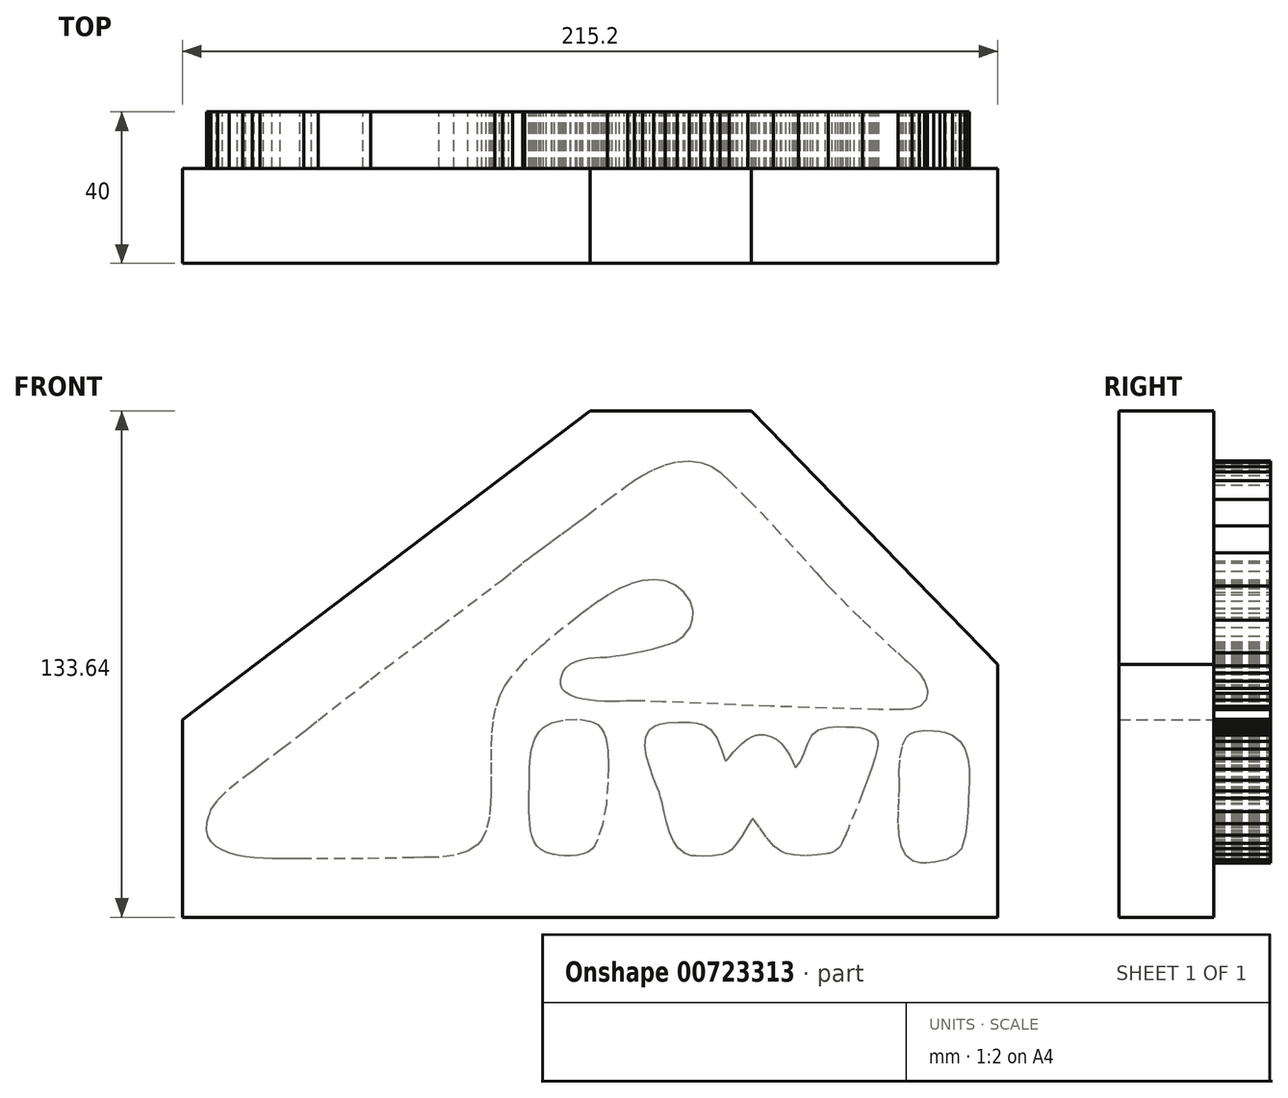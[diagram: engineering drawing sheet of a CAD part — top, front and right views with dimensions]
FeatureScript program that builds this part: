
annotation { "Feature Type Name" : "Feature", "Feature Type Description" : "" }
export const myFeature = defineFeature(function(context is Context, id is Id, definition is map)
    precondition{}
    {
        {
            var Q0;
            Q0=qCreatedBy(makeId("Front.planeOp"),FACE);
            var sketch = newSketch(context, id + "F0", { "sketchPlane" : qUnion([Q0])});
            skLineSegment(sketch, "E0", {"start": v(-15.49, -29.13) * mm, "end": v(-15.48, -28.37) * mm});
            skLineSegment(sketch, "E1", {"start": v(-15.48, -28.37) * mm, "end": v(-15.38, -26.1) * mm});
            skLineSegment(sketch, "E2", {"start": v(-15.38, -26.1) * mm, "end": v(-15, -23.12) * mm});
            skLineSegment(sketch, "E3", {"start": v(-15, -23.12) * mm, "end": v(-14.07, -20.33) * mm});
            skLineSegment(sketch, "E4", {"start": v(-14.07, -20.33) * mm, "end": v(-12.87, -18.4) * mm});
            skLineSegment(sketch, "E5", {"start": v(-12.87, -18.4) * mm, "end": v(-12.36, -17.88) * mm});
            skLineSegment(sketch, "E6", {"start": v(-12.36, -17.88) * mm, "end": v(-11.78, -17.29) * mm});
            skLineSegment(sketch, "E7", {"start": v(-11.78, -17.29) * mm, "end": v(-9.5, -16.05) * mm});
            skLineSegment(sketch, "E8", {"start": v(-9.5, -16.05) * mm, "end": v(-5.9, -15.18) * mm});
            skLineSegment(sketch, "E9", {"start": v(-5.9, -15.18) * mm, "end": v(-2.13, -15.15) * mm});
            skLineSegment(sketch, "E10", {"start": v(-2.13, -15.15) * mm, "end": v(0.44, -15.56) * mm});
            skLineSegment(sketch, "E11", {"start": v(0.44, -15.56) * mm, "end": v(1.25, -15.83) * mm});
            skLineSegment(sketch, "E12", {"start": v(1.25, -15.83) * mm, "end": v(1.59, -15.94) * mm});
            skLineSegment(sketch, "E13", {"start": v(1.59, -15.94) * mm, "end": v(2.5, -16.5) * mm});
            skLineSegment(sketch, "E14", {"start": v(2.5, -16.5) * mm, "end": v(3.48, -17.52) * mm});
            skLineSegment(sketch, "E15", {"start": v(3.48, -17.52) * mm, "end": v(4.2, -18.8) * mm});
            skLineSegment(sketch, "E16", {"start": v(4.2, -18.8) * mm, "end": v(4.7, -20.25) * mm});
            skLineSegment(sketch, "E17", {"start": v(4.7, -20.25) * mm, "end": v(5.02, -21.82) * mm});
            skLineSegment(sketch, "E18", {"start": v(5.02, -21.82) * mm, "end": v(5.2, -23.41) * mm});
            skLineSegment(sketch, "E19", {"start": v(5.2, -23.41) * mm, "end": v(5.3, -24.95) * mm});
            skLineSegment(sketch, "E20", {"start": v(5.3, -24.95) * mm, "end": v(5.32, -26) * mm});
            skLineSegment(sketch, "E21", {"start": v(5.32, -26) * mm, "end": v(5.32, -26.35) * mm});
            skLineSegment(sketch, "E22", {"start": v(5.32, -26.35) * mm, "end": v(5.32, -27.7) * mm});
            skLineSegment(sketch, "E23", {"start": v(5.32, -27.7) * mm, "end": v(5.23, -31.79) * mm});
            skLineSegment(sketch, "E24", {"start": v(5.23, -31.79) * mm, "end": v(4.8, -37.42) * mm});
            skLineSegment(sketch, "E25", {"start": v(4.8, -37.42) * mm, "end": v(3.78, -42.93) * mm});
            skLineSegment(sketch, "E26", {"start": v(3.78, -42.93) * mm, "end": v(2.53, -46.82) * mm});
            skLineSegment(sketch, "E27", {"start": v(2.53, -46.82) * mm, "end": v(1.95, -48.03) * mm});
            skLineSegment(sketch, "E28", {"start": v(1.95, -48.03) * mm, "end": v(1.8, -48.36) * mm});
            skLineSegment(sketch, "E29", {"start": v(1.8, -48.36) * mm, "end": v(1.11, -49.23) * mm});
            skLineSegment(sketch, "E30", {"start": v(1.11, -49.23) * mm, "end": v(-0.02, -50.1) * mm});
            skLineSegment(sketch, "E31", {"start": v(-0.02, -50.1) * mm, "end": v(-1.38, -50.7) * mm});
            skLineSegment(sketch, "E32", {"start": v(-1.38, -50.7) * mm, "end": v(-2.9, -51.06) * mm});
            skLineSegment(sketch, "E33", {"start": v(-2.9, -51.06) * mm, "end": v(-4.5, -51.2) * mm});
            skLineSegment(sketch, "E34", {"start": v(-4.5, -51.2) * mm, "end": v(-6.14, -51.18) * mm});
            skLineSegment(sketch, "E35", {"start": v(-6.14, -51.18) * mm, "end": v(-7.74, -51.03) * mm});
            skLineSegment(sketch, "E36", {"start": v(-7.74, -51.03) * mm, "end": v(-8.85, -50.86) * mm});
            skLineSegment(sketch, "E37", {"start": v(-8.85, -50.86) * mm, "end": v(-9.21, -50.79) * mm});
            skLineSegment(sketch, "E38", {"start": v(-9.21, -50.79) * mm, "end": v(-9.68, -50.7) * mm});
            skLineSegment(sketch, "E39", {"start": v(-9.68, -50.7) * mm, "end": v(-11.03, -50.25) * mm});
            skLineSegment(sketch, "E40", {"start": v(-11.03, -50.25) * mm, "end": v(-12.44, -49.48) * mm});
            skLineSegment(sketch, "E41", {"start": v(-12.44, -49.48) * mm, "end": v(-13.5, -48.48) * mm});
            skLineSegment(sketch, "E42", {"start": v(-13.5, -48.48) * mm, "end": v(-14.28, -47.28) * mm});
            skLineSegment(sketch, "E43", {"start": v(-14.28, -47.28) * mm, "end": v(-14.82, -45.9) * mm});
            skLineSegment(sketch, "E44", {"start": v(-14.82, -45.9) * mm, "end": v(-15.16, -44.37) * mm});
            skLineSegment(sketch, "E45", {"start": v(-15.16, -44.37) * mm, "end": v(-15.37, -42.7) * mm});
            skLineSegment(sketch, "E46", {"start": v(-15.37, -42.7) * mm, "end": v(-15.48, -41.36) * mm});
            skLineSegment(sketch, "E47", {"start": v(-15.48, -41.36) * mm, "end": v(-15.5, -40.9) * mm});
            skLineSegment(sketch, "E48", {"start": v(-15.5, -40.9) * mm, "end": v(-15.52, -40.68) * mm});
            skLineSegment(sketch, "E49", {"start": v(-15.52, -40.68) * mm, "end": v(-15.53, -39.98) * mm});
            skLineSegment(sketch, "E50", {"start": v(-15.53, -39.98) * mm, "end": v(-15.54, -38.53) * mm});
            skLineSegment(sketch, "E51", {"start": v(-15.54, -38.53) * mm, "end": v(-15.54, -36.74) * mm});
            skLineSegment(sketch, "E52", {"start": v(-15.54, -36.74) * mm, "end": v(-15.54, -34.79) * mm});
            skLineSegment(sketch, "E53", {"start": v(-15.54, -34.79) * mm, "end": v(-15.52, -32.86) * mm});
            skLineSegment(sketch, "E54", {"start": v(-15.52, -32.86) * mm, "end": v(-15.51, -31.16) * mm});
            skLineSegment(sketch, "E55", {"start": v(-15.51, -31.16) * mm, "end": v(-15.5, -29.85) * mm});
            skLineSegment(sketch, "E56", {"start": v(-15.5, -29.85) * mm, "end": v(-15.49, -29.3) * mm});
            skLineSegment(sketch, "E57", {"start": v(-15.49, -29.3) * mm, "end": v(-15.49, -29.13) * mm});
            skLineSegment(sketch, "E58", {"start": v(84.47, -19.48) * mm, "end": v(84.82, -19.11) * mm});
            skLineSegment(sketch, "E59", {"start": v(84.82, -19.11) * mm, "end": v(86.32, -18.4) * mm});
            skLineSegment(sketch, "E60", {"start": v(86.32, -18.4) * mm, "end": v(88.7, -18.05) * mm});
            skLineSegment(sketch, "E61", {"start": v(88.7, -18.05) * mm, "end": v(91.21, -18.14) * mm});
            skLineSegment(sketch, "E62", {"start": v(91.21, -18.14) * mm, "end": v(92.88, -18.35) * mm});
            skLineSegment(sketch, "E63", {"start": v(92.88, -18.35) * mm, "end": v(93.44, -18.43) * mm});
            skLineSegment(sketch, "E64", {"start": v(93.44, -18.43) * mm, "end": v(94.15, -18.54) * mm});
            skLineSegment(sketch, "E65", {"start": v(94.15, -18.54) * mm, "end": v(96.21, -19.32) * mm});
            skLineSegment(sketch, "E66", {"start": v(96.21, -19.32) * mm, "end": v(98.19, -20.9) * mm});
            skLineSegment(sketch, "E67", {"start": v(98.19, -20.9) * mm, "end": v(99.5, -23.04) * mm});
            skLineSegment(sketch, "E68", {"start": v(99.5, -23.04) * mm, "end": v(100.25, -25.57) * mm});
            skLineSegment(sketch, "E69", {"start": v(100.25, -25.57) * mm, "end": v(100.6, -28.34) * mm});
            skLineSegment(sketch, "E70", {"start": v(100.6, -28.34) * mm, "end": v(100.65, -31.19) * mm});
            skLineSegment(sketch, "E71", {"start": v(100.65, -31.19) * mm, "end": v(100.54, -33.97) * mm});
            skLineSegment(sketch, "E72", {"start": v(100.54, -33.97) * mm, "end": v(100.43, -35.9) * mm});
            skLineSegment(sketch, "E73", {"start": v(100.43, -35.9) * mm, "end": v(100.4, -36.54) * mm});
            skLineSegment(sketch, "E74", {"start": v(100.4, -36.54) * mm, "end": v(100.36, -37.28) * mm});
            skLineSegment(sketch, "E75", {"start": v(100.36, -37.28) * mm, "end": v(100.25, -39.52) * mm});
            skLineSegment(sketch, "E76", {"start": v(100.25, -39.52) * mm, "end": v(100.02, -42.64) * mm});
            skLineSegment(sketch, "E77", {"start": v(100.02, -42.64) * mm, "end": v(99.57, -45.71) * mm});
            skLineSegment(sketch, "E78", {"start": v(99.57, -45.71) * mm, "end": v(99.03, -47.89) * mm});
            skLineSegment(sketch, "E79", {"start": v(99.03, -47.89) * mm, "end": v(98.76, -48.58) * mm});
            skLineSegment(sketch, "E80", {"start": v(98.76, -48.58) * mm, "end": v(98.52, -49.22) * mm});
            skLineSegment(sketch, "E81", {"start": v(98.52, -49.22) * mm, "end": v(97.1, -50.85) * mm});
            skLineSegment(sketch, "E82", {"start": v(97.1, -50.85) * mm, "end": v(94.51, -52.21) * mm});
            skLineSegment(sketch, "E83", {"start": v(94.51, -52.21) * mm, "end": v(91.5, -52.89) * mm});
            skLineSegment(sketch, "E84", {"start": v(91.5, -52.89) * mm, "end": v(89.28, -53.08) * mm});
            skLineSegment(sketch, "E85", {"start": v(89.28, -53.08) * mm, "end": v(88.53, -53.1) * mm});
            skLineSegment(sketch, "E86", {"start": v(88.53, -53.1) * mm, "end": v(87.84, -53.11) * mm});
            skLineSegment(sketch, "E87", {"start": v(87.84, -53.11) * mm, "end": v(85.76, -52.58) * mm});
            skLineSegment(sketch, "E88", {"start": v(85.76, -52.58) * mm, "end": v(83.87, -51.05) * mm});
            skLineSegment(sketch, "E89", {"start": v(83.87, -51.05) * mm, "end": v(82.7, -48.7) * mm});
            skLineSegment(sketch, "E90", {"start": v(82.7, -48.7) * mm, "end": v(82.08, -45.78) * mm});
            skLineSegment(sketch, "E91", {"start": v(82.08, -45.78) * mm, "end": v(81.87, -42.5) * mm});
            skLineSegment(sketch, "E92", {"start": v(81.87, -42.5) * mm, "end": v(81.92, -39.06) * mm});
            skLineSegment(sketch, "E93", {"start": v(81.92, -39.06) * mm, "end": v(82.06, -35.7) * mm});
            skLineSegment(sketch, "E94", {"start": v(82.06, -35.7) * mm, "end": v(82.14, -33.41) * mm});
            skLineSegment(sketch, "E95", {"start": v(82.14, -33.41) * mm, "end": v(82.14, -32.65) * mm});
            skLineSegment(sketch, "E96", {"start": v(82.14, -32.65) * mm, "end": v(82.14, -31.7) * mm});
            skLineSegment(sketch, "E97", {"start": v(82.14, -31.7) * mm, "end": v(82.13, -28.87) * mm});
            skLineSegment(sketch, "E98", {"start": v(82.13, -28.87) * mm, "end": v(82.31, -25.24) * mm});
            skLineSegment(sketch, "E99", {"start": v(82.31, -25.24) * mm, "end": v(83, -22.02) * mm});
            skLineSegment(sketch, "E100", {"start": v(83, -22.02) * mm, "end": v(83.98, -20) * mm});
            skLineSegment(sketch, "E101", {"start": v(83.98, -20) * mm, "end": v(84.47, -19.48) * mm});
            skLineSegment(sketch, "E102", {"start": v(27.66, 13.43) * mm, "end": v(27.59, 14.13) * mm});
            skLineSegment(sketch, "E103", {"start": v(27.59, 14.13) * mm, "end": v(26.9, 16.16) * mm});
            skLineSegment(sketch, "E104", {"start": v(26.9, 16.16) * mm, "end": v(25.36, 18.47) * mm});
            skLineSegment(sketch, "E105", {"start": v(25.36, 18.47) * mm, "end": v(23.2, 20.21) * mm});
            skLineSegment(sketch, "E106", {"start": v(23.2, 20.21) * mm, "end": v(21.25, 21.11) * mm});
            skLineSegment(sketch, "E107", {"start": v(21.25, 21.11) * mm, "end": v(20.57, 21.27) * mm});
            skLineSegment(sketch, "E108", {"start": v(20.57, 21.27) * mm, "end": v(19.79, 21.46) * mm});
            skLineSegment(sketch, "E109", {"start": v(19.79, 21.46) * mm, "end": v(17.37, 21.68) * mm});
            skLineSegment(sketch, "E110", {"start": v(17.37, 21.68) * mm, "end": v(14.24, 21.42) * mm});
            skLineSegment(sketch, "E111", {"start": v(14.24, 21.42) * mm, "end": v(11.22, 20.61) * mm});
            skLineSegment(sketch, "E112", {"start": v(11.22, 20.61) * mm, "end": v(8.3, 19.37) * mm});
            skLineSegment(sketch, "E113", {"start": v(8.3, 19.37) * mm, "end": v(5.49, 17.82) * mm});
            skLineSegment(sketch, "E114", {"start": v(5.49, 17.82) * mm, "end": v(2.8, 16.08) * mm});
            skLineSegment(sketch, "E115", {"start": v(2.8, 16.08) * mm, "end": v(0.27, 14.25) * mm});
            skLineSegment(sketch, "E116", {"start": v(0.27, 14.25) * mm, "end": v(-1.51, 12.91) * mm});
            skLineSegment(sketch, "E117", {"start": v(-1.51, 12.91) * mm, "end": v(-2.1, 12.46) * mm});
            skLineSegment(sketch, "E118", {"start": v(-2.1, 12.46) * mm, "end": v(-2.94, 11.84) * mm});
            skLineSegment(sketch, "E119", {"start": v(-2.94, 11.84) * mm, "end": v(-11.04, 5.29) * mm});
            skLineSegment(sketch, "E120", {"start": v(-11.04, 5.29) * mm, "end": v(-11.83, 4.63) * mm});
            skLineSegment(sketch, "E121", {"start": v(-11.83, 4.63) * mm, "end": v(-12.72, 3.9) * mm});
            skLineSegment(sketch, "E122", {"start": v(-12.72, 3.9) * mm, "end": v(-17.1, -0.15) * mm});
            skLineSegment(sketch, "E123", {"start": v(-17.1, -0.15) * mm, "end": v(-20.97, -4.65) * mm});
            skLineSegment(sketch, "E124", {"start": v(-20.97, -4.65) * mm, "end": v(-21.6, -5.62) * mm});
            skLineSegment(sketch, "E125", {"start": v(-21.6, -5.62) * mm, "end": v(-22.09, -6.38) * mm});
            skLineSegment(sketch, "E126", {"start": v(-22.09, -6.38) * mm, "end": v(-23.3, -8.85) * mm});
            skLineSegment(sketch, "E127", {"start": v(-23.3, -8.85) * mm, "end": v(-24.46, -12.24) * mm});
            skLineSegment(sketch, "E128", {"start": v(-24.46, -12.24) * mm, "end": v(-25.16, -15.74) * mm});
            skLineSegment(sketch, "E129", {"start": v(-25.16, -15.74) * mm, "end": v(-25.52, -19.33) * mm});
            skLineSegment(sketch, "E130", {"start": v(-25.52, -19.33) * mm, "end": v(-25.63, -22.96) * mm});
            skLineSegment(sketch, "E131", {"start": v(-25.63, -22.96) * mm, "end": v(-25.61, -26.6) * mm});
            skLineSegment(sketch, "E132", {"start": v(-25.61, -26.6) * mm, "end": v(-25.57, -30.23) * mm});
            skLineSegment(sketch, "E133", {"start": v(-25.57, -30.23) * mm, "end": v(-25.59, -32.9) * mm});
            skLineSegment(sketch, "E134", {"start": v(-25.59, -32.9) * mm, "end": v(-25.62, -33.79) * mm});
            skLineSegment(sketch, "E135", {"start": v(-25.62, -33.79) * mm, "end": v(-25.65, -34.66) * mm});
            skLineSegment(sketch, "E136", {"start": v(-25.65, -34.66) * mm, "end": v(-25.73, -37.29) * mm});
            skLineSegment(sketch, "E137", {"start": v(-25.73, -37.29) * mm, "end": v(-26.05, -40.94) * mm});
            skLineSegment(sketch, "E138", {"start": v(-26.05, -40.94) * mm, "end": v(-26.9, -44.44) * mm});
            skLineSegment(sketch, "E139", {"start": v(-26.9, -44.44) * mm, "end": v(-28.06, -46.83) * mm});
            skLineSegment(sketch, "E140", {"start": v(-28.06, -46.83) * mm, "end": v(-28.6, -47.5) * mm});
            skLineSegment(sketch, "E141", {"start": v(-28.6, -47.5) * mm, "end": v(-29.2, -48.23) * mm});
            skLineSegment(sketch, "E142", {"start": v(-29.2, -48.23) * mm, "end": v(-31.67, -49.9) * mm});
            skLineSegment(sketch, "E143", {"start": v(-31.67, -49.9) * mm, "end": v(-35.39, -51.1) * mm});
            skLineSegment(sketch, "E144", {"start": v(-35.39, -51.1) * mm, "end": v(-39.38, -51.5) * mm});
            skLineSegment(sketch, "E145", {"start": v(-39.38, -51.5) * mm, "end": v(-42.28, -51.59) * mm});
            skLineSegment(sketch, "E146", {"start": v(-42.28, -51.59) * mm, "end": v(-43.25, -51.62) * mm});
            skLineSegment(sketch, "E147", {"start": v(-43.25, -51.62) * mm, "end": v(-45.96, -51.7) * mm});
            skLineSegment(sketch, "E148", {"start": v(-45.96, -51.7) * mm, "end": v(-59.46, -51.96) * mm});
            skLineSegment(sketch, "E149", {"start": v(-59.46, -51.96) * mm, "end": v(-72.97, -52) * mm});
            skLineSegment(sketch, "E150", {"start": v(-72.97, -52) * mm, "end": v(-75.69, -51.95) * mm});
            skLineSegment(sketch, "E151", {"start": v(-75.69, -51.95) * mm, "end": v(-76.08, -51.94) * mm});
            skLineSegment(sketch, "E152", {"start": v(-76.08, -51.94) * mm, "end": v(-77.27, -51.94) * mm});
            skLineSegment(sketch, "E153", {"start": v(-77.27, -51.94) * mm, "end": v(-79.12, -51.96) * mm});
            skLineSegment(sketch, "E154", {"start": v(-79.12, -51.96) * mm, "end": v(-81.2, -51.96) * mm});
            skLineSegment(sketch, "E155", {"start": v(-81.2, -51.96) * mm, "end": v(-83.41, -51.93) * mm});
            skLineSegment(sketch, "E156", {"start": v(-83.41, -51.93) * mm, "end": v(-85.72, -51.85) * mm});
            skLineSegment(sketch, "E157", {"start": v(-85.72, -51.85) * mm, "end": v(-88.06, -51.68) * mm});
            skLineSegment(sketch, "E158", {"start": v(-88.06, -51.68) * mm, "end": v(-90.38, -51.4) * mm});
            skLineSegment(sketch, "E159", {"start": v(-90.38, -51.4) * mm, "end": v(-92.6, -51) * mm});
            skLineSegment(sketch, "E160", {"start": v(-92.6, -51) * mm, "end": v(-94.67, -50.43) * mm});
            skLineSegment(sketch, "E161", {"start": v(-94.67, -50.43) * mm, "end": v(-96.53, -49.69) * mm});
            skLineSegment(sketch, "E162", {"start": v(-96.53, -49.69) * mm, "end": v(-98.12, -48.73) * mm});
            skLineSegment(sketch, "E163", {"start": v(-98.12, -48.73) * mm, "end": v(-99.38, -47.54) * mm});
            skLineSegment(sketch, "E164", {"start": v(-99.38, -47.54) * mm, "end": v(-100.24, -46.1) * mm});
            skLineSegment(sketch, "E165", {"start": v(-100.24, -46.1) * mm, "end": v(-100.65, -44.37) * mm});
            skLineSegment(sketch, "E166", {"start": v(-100.65, -44.37) * mm, "end": v(-100.54, -42.34) * mm});
            skLineSegment(sketch, "E167", {"start": v(-100.54, -42.34) * mm, "end": v(-100.08, -40.55) * mm});
            skLineSegment(sketch, "E168", {"start": v(-100.08, -40.55) * mm, "end": v(-99.85, -39.98) * mm});
            skLineSegment(sketch, "E169", {"start": v(-99.85, -39.98) * mm, "end": v(-99.48, -39.02) * mm});
            skLineSegment(sketch, "E170", {"start": v(-99.48, -39.02) * mm, "end": v(-97.72, -36.4) * mm});
            skLineSegment(sketch, "E171", {"start": v(-97.72, -36.4) * mm, "end": v(-94.67, -33.35) * mm});
            skLineSegment(sketch, "E172", {"start": v(-94.67, -33.35) * mm, "end": v(-91.2, -30.65) * mm});
            skLineSegment(sketch, "E173", {"start": v(-91.2, -30.65) * mm, "end": v(-88.62, -28.77) * mm});
            skLineSegment(sketch, "E174", {"start": v(-88.62, -28.77) * mm, "end": v(-87.78, -28.12) * mm});
            skLineSegment(sketch, "E175", {"start": v(-87.78, -28.12) * mm, "end": v(-86.64, -27.23) * mm});
            skLineSegment(sketch, "E176", {"start": v(-86.64, -27.23) * mm, "end": v(-80.82, -22.86) * mm});
            skLineSegment(sketch, "E177", {"start": v(-80.82, -22.86) * mm, "end": v(-75.05, -18.44) * mm});
            skLineSegment(sketch, "E178", {"start": v(-75.05, -18.44) * mm, "end": v(-73.92, -17.53) * mm});
            skLineSegment(sketch, "E179", {"start": v(-73.92, -17.53) * mm, "end": v(-71.2, -15.32) * mm});
            skLineSegment(sketch, "E180", {"start": v(-71.2, -15.32) * mm, "end": v(-57.33, -4.54) * mm});
            skLineSegment(sketch, "E181", {"start": v(-57.33, -4.54) * mm, "end": v(-43.32, 6.08) * mm});
            skLineSegment(sketch, "E182", {"start": v(-43.32, 6.08) * mm, "end": v(-40.53, 8.2) * mm});
            skLineSegment(sketch, "E183", {"start": v(-40.53, 8.2) * mm, "end": v(-39.08, 9.3) * mm});
            skLineSegment(sketch, "E184", {"start": v(-39.08, 9.3) * mm, "end": v(-24.57, 20.28) * mm});
            skLineSegment(sketch, "E185", {"start": v(-24.57, 20.28) * mm, "end": v(-23.11, 21.36) * mm});
            skLineSegment(sketch, "E186", {"start": v(-23.11, 21.36) * mm, "end": v(-22.6, 21.74) * mm});
            skLineSegment(sketch, "E187", {"start": v(-22.6, 21.74) * mm, "end": v(-19.85, 23.99) * mm});
            skLineSegment(sketch, "E188", {"start": v(-19.85, 23.99) * mm, "end": v(-17.28, 26.15) * mm});
            skLineSegment(sketch, "E189", {"start": v(-17.28, 26.15) * mm, "end": v(-16.85, 26.48) * mm});
            skLineSegment(sketch, "E190", {"start": v(-16.85, 26.48) * mm, "end": v(-16.69, 26.6) * mm});
            skLineSegment(sketch, "E191", {"start": v(-16.69, 26.6) * mm, "end": v(-16.08, 27.06) * mm});
            skLineSegment(sketch, "E192", {"start": v(-16.08, 27.06) * mm, "end": v(-14.42, 28.29) * mm});
            skLineSegment(sketch, "E193", {"start": v(-14.42, 28.29) * mm, "end": v(-12.16, 29.95) * mm});
            skLineSegment(sketch, "E194", {"start": v(-12.16, 29.95) * mm, "end": v(-9.57, 31.86) * mm});
            skLineSegment(sketch, "E195", {"start": v(-9.57, 31.86) * mm, "end": v(-6.91, 33.82) * mm});
            skLineSegment(sketch, "E196", {"start": v(-6.91, 33.82) * mm, "end": v(-4.46, 35.62) * mm});
            skLineSegment(sketch, "E197", {"start": v(-4.46, 35.62) * mm, "end": v(-2.5, 37.07) * mm});
            skLineSegment(sketch, "E198", {"start": v(-2.5, 37.07) * mm, "end": v(-1.59, 37.74) * mm});
            skLineSegment(sketch, "E199", {"start": v(-1.59, 37.74) * mm, "end": v(-1.29, 37.97) * mm});
            skLineSegment(sketch, "E200", {"start": v(-1.29, 37.97) * mm, "end": v(-0.21, 38.77) * mm});
            skLineSegment(sketch, "E201", {"start": v(-0.21, 38.77) * mm, "end": v(5.1, 42.8) * mm});
            skLineSegment(sketch, "E202", {"start": v(5.1, 42.8) * mm, "end": v(10.48, 46.73) * mm});
            skLineSegment(sketch, "E203", {"start": v(10.48, 46.73) * mm, "end": v(11.6, 47.48) * mm});
            skLineSegment(sketch, "E204", {"start": v(11.6, 47.48) * mm, "end": v(12.27, 47.94) * mm});
            skLineSegment(sketch, "E205", {"start": v(12.27, 47.94) * mm, "end": v(14.38, 49.24) * mm});
            skLineSegment(sketch, "E206", {"start": v(14.38, 49.24) * mm, "end": v(17.34, 50.79) * mm});
            skLineSegment(sketch, "E207", {"start": v(17.34, 50.79) * mm, "end": v(20.41, 52.03) * mm});
            skLineSegment(sketch, "E208", {"start": v(20.41, 52.03) * mm, "end": v(23.55, 52.84) * mm});
            skLineSegment(sketch, "E209", {"start": v(23.55, 52.84) * mm, "end": v(26.68, 53.11) * mm});
            skLineSegment(sketch, "E210", {"start": v(26.68, 53.11) * mm, "end": v(29.75, 52.73) * mm});
            skLineSegment(sketch, "E211", {"start": v(29.75, 52.73) * mm, "end": v(32.7, 51.58) * mm});
            skLineSegment(sketch, "E212", {"start": v(32.7, 51.58) * mm, "end": v(34.83, 50.14) * mm});
            skLineSegment(sketch, "E213", {"start": v(34.83, 50.14) * mm, "end": v(35.45, 49.56) * mm});
            skLineSegment(sketch, "E214", {"start": v(35.45, 49.56) * mm, "end": v(37.18, 47.92) * mm});
            skLineSegment(sketch, "E215", {"start": v(37.18, 47.92) * mm, "end": v(42.25, 42.88) * mm});
            skLineSegment(sketch, "E216", {"start": v(42.25, 42.88) * mm, "end": v(48.96, 35.9) * mm});
            skLineSegment(sketch, "E217", {"start": v(48.96, 35.9) * mm, "end": v(55.5, 28.84) * mm});
            skLineSegment(sketch, "E218", {"start": v(55.5, 28.84) * mm, "end": v(60.2, 23.62) * mm});
            skLineSegment(sketch, "E219", {"start": v(60.2, 23.62) * mm, "end": v(61.77, 21.88) * mm});
            skLineSegment(sketch, "E220", {"start": v(61.77, 21.88) * mm, "end": v(63.44, 20.02) * mm});
            skLineSegment(sketch, "E221", {"start": v(63.44, 20.02) * mm, "end": v(72.41, 11) * mm});
            skLineSegment(sketch, "E222", {"start": v(72.41, 11) * mm, "end": v(81.77, 2.35) * mm});
            skLineSegment(sketch, "E223", {"start": v(81.77, 2.35) * mm, "end": v(83.63, 0.68) * mm});
            skLineSegment(sketch, "E224", {"start": v(83.63, 0.68) * mm, "end": v(84.11, 0.25) * mm});
            skLineSegment(sketch, "E225", {"start": v(84.11, 0.25) * mm, "end": v(85.56, -1.06) * mm});
            skLineSegment(sketch, "E226", {"start": v(85.56, -1.06) * mm, "end": v(87.4, -2.98) * mm});
            skLineSegment(sketch, "E227", {"start": v(87.4, -2.98) * mm, "end": v(88.82, -5.14) * mm});
            skLineSegment(sketch, "E228", {"start": v(88.82, -5.14) * mm, "end": v(89.47, -7) * mm});
            skLineSegment(sketch, "E229", {"start": v(89.47, -7) * mm, "end": v(89.53, -7.63) * mm});
            skLineSegment(sketch, "E230", {"start": v(89.53, -7.63) * mm, "end": v(89.59, -8.23) * mm});
            skLineSegment(sketch, "E231", {"start": v(89.59, -8.23) * mm, "end": v(89.16, -10.1) * mm});
            skLineSegment(sketch, "E232", {"start": v(89.16, -10.1) * mm, "end": v(87.68, -11.63) * mm});
            skLineSegment(sketch, "E233", {"start": v(87.68, -11.63) * mm, "end": v(85.37, -12.4) * mm});
            skLineSegment(sketch, "E234", {"start": v(85.37, -12.4) * mm, "end": v(83.22, -12.62) * mm});
            skLineSegment(sketch, "E235", {"start": v(83.22, -12.62) * mm, "end": v(82.51, -12.61) * mm});
            skLineSegment(sketch, "E236", {"start": v(82.51, -12.61) * mm, "end": v(76.8, -12.56) * mm});
            skLineSegment(sketch, "E237", {"start": v(76.8, -12.56) * mm, "end": v(48.17, -11.7) * mm});
            skLineSegment(sketch, "E238", {"start": v(48.17, -11.7) * mm, "end": v(19.58, -10.48) * mm});
            skLineSegment(sketch, "E239", {"start": v(19.58, -10.48) * mm, "end": v(13.87, -10.26) * mm});
            skLineSegment(sketch, "E240", {"start": v(13.87, -10.26) * mm, "end": v(13.63, -10.25) * mm});
            skLineSegment(sketch, "E241", {"start": v(13.63, -10.25) * mm, "end": v(12.9, -10.26) * mm});
            skLineSegment(sketch, "E242", {"start": v(12.9, -10.26) * mm, "end": v(11.61, -10.29) * mm});
            skLineSegment(sketch, "E243", {"start": v(11.61, -10.29) * mm, "end": v(10.05, -10.33) * mm});
            skLineSegment(sketch, "E244", {"start": v(10.05, -10.33) * mm, "end": v(8.29, -10.37) * mm});
            skLineSegment(sketch, "E245", {"start": v(8.29, -10.37) * mm, "end": v(6.38, -10.39) * mm});
            skLineSegment(sketch, "E246", {"start": v(6.38, -10.39) * mm, "end": v(4.38, -10.35) * mm});
            skLineSegment(sketch, "E247", {"start": v(4.38, -10.35) * mm, "end": v(2.37, -10.25) * mm});
            skLineSegment(sketch, "E248", {"start": v(2.37, -10.25) * mm, "end": v(0.4, -10.07) * mm});
            skLineSegment(sketch, "E249", {"start": v(0.4, -10.07) * mm, "end": v(-1.48, -9.77) * mm});
            skLineSegment(sketch, "E250", {"start": v(-1.48, -9.77) * mm, "end": v(-3.2, -9.34) * mm});
            skLineSegment(sketch, "E251", {"start": v(-3.2, -9.34) * mm, "end": v(-4.7, -8.77) * mm});
            skLineSegment(sketch, "E252", {"start": v(-4.7, -8.77) * mm, "end": v(-5.9, -8.02) * mm});
            skLineSegment(sketch, "E253", {"start": v(-5.9, -8.02) * mm, "end": v(-6.77, -7.08) * mm});
            skLineSegment(sketch, "E254", {"start": v(-6.77, -7.08) * mm, "end": v(-7.24, -5.93) * mm});
            skLineSegment(sketch, "E255", {"start": v(-7.24, -5.93) * mm, "end": v(-7.24, -4.54) * mm});
            skLineSegment(sketch, "E256", {"start": v(-7.24, -4.54) * mm, "end": v(-6.88, -3.3) * mm});
            skLineSegment(sketch, "E257", {"start": v(-6.88, -3.3) * mm, "end": v(-6.7, -2.9) * mm});
            skLineSegment(sketch, "E258", {"start": v(-6.7, -2.9) * mm, "end": v(-6.54, -2.54) * mm});
            skLineSegment(sketch, "E259", {"start": v(-6.54, -2.54) * mm, "end": v(-5.82, -1.54) * mm});
            skLineSegment(sketch, "E260", {"start": v(-5.82, -1.54) * mm, "end": v(-4.63, -0.53) * mm});
            skLineSegment(sketch, "E261", {"start": v(-4.63, -0.53) * mm, "end": v(-3.22, 0.18) * mm});
            skLineSegment(sketch, "E262", {"start": v(-3.22, 0.18) * mm, "end": v(-1.65, 0.66) * mm});
            skLineSegment(sketch, "E263", {"start": v(-1.65, 0.66) * mm, "end": v(0, 0.95) * mm});
            skLineSegment(sketch, "E264", {"start": v(0, 0.95) * mm, "end": v(1.66, 1.12) * mm});
            skLineSegment(sketch, "E265", {"start": v(1.66, 1.12) * mm, "end": v(3.27, 1.2) * mm});
            skLineSegment(sketch, "E266", {"start": v(3.27, 1.2) * mm, "end": v(4.37, 1.26) * mm});
            skLineSegment(sketch, "E267", {"start": v(4.37, 1.26) * mm, "end": v(4.73, 1.28) * mm});
            skLineSegment(sketch, "E268", {"start": v(4.73, 1.28) * mm, "end": v(4.99, 1.3) * mm});
            skLineSegment(sketch, "E269", {"start": v(4.99, 1.3) * mm, "end": v(5.75, 1.38) * mm});
            skLineSegment(sketch, "E270", {"start": v(5.75, 1.38) * mm, "end": v(7.42, 1.6) * mm});
            skLineSegment(sketch, "E271", {"start": v(7.42, 1.6) * mm, "end": v(9.57, 1.95) * mm});
            skLineSegment(sketch, "E272", {"start": v(9.57, 1.95) * mm, "end": v(12.05, 2.4) * mm});
            skLineSegment(sketch, "E273", {"start": v(12.05, 2.4) * mm, "end": v(14.72, 2.93) * mm});
            skLineSegment(sketch, "E274", {"start": v(14.72, 2.93) * mm, "end": v(17.4, 3.56) * mm});
            skLineSegment(sketch, "E275", {"start": v(17.4, 3.56) * mm, "end": v(19.95, 4.26) * mm});
            skLineSegment(sketch, "E276", {"start": v(19.95, 4.26) * mm, "end": v(21.66, 4.81) * mm});
            skLineSegment(sketch, "E277", {"start": v(21.66, 4.81) * mm, "end": v(22.21, 5.03) * mm});
            skLineSegment(sketch, "E278", {"start": v(22.21, 5.03) * mm, "end": v(23.02, 5.34) * mm});
            skLineSegment(sketch, "E279", {"start": v(23.02, 5.34) * mm, "end": v(25.22, 6.83) * mm});
            skLineSegment(sketch, "E280", {"start": v(25.22, 6.83) * mm, "end": v(26.92, 9.08) * mm});
            skLineSegment(sketch, "E281", {"start": v(26.92, 9.08) * mm, "end": v(27.63, 11.4) * mm});
            skLineSegment(sketch, "E282", {"start": v(27.63, 11.4) * mm, "end": v(27.72, 12.93) * mm});
            skLineSegment(sketch, "E283", {"start": v(27.72, 12.93) * mm, "end": v(27.66, 13.43) * mm});
            skLineSegment(sketch, "E284", {"start": v(44.68, -19.27) * mm, "end": v(45.14, -19.2) * mm});
            skLineSegment(sketch, "E285", {"start": v(45.14, -19.2) * mm, "end": v(46.56, -19.2) * mm});
            skLineSegment(sketch, "E286", {"start": v(46.56, -19.2) * mm, "end": v(48.25, -19.64) * mm});
            skLineSegment(sketch, "E287", {"start": v(48.25, -19.64) * mm, "end": v(49.77, -20.48) * mm});
            skLineSegment(sketch, "E288", {"start": v(49.77, -20.48) * mm, "end": v(51.1, -21.65) * mm});
            skLineSegment(sketch, "E289", {"start": v(51.1, -21.65) * mm, "end": v(52.25, -23.06) * mm});
            skLineSegment(sketch, "E290", {"start": v(52.25, -23.06) * mm, "end": v(53.22, -24.62) * mm});
            skLineSegment(sketch, "E291", {"start": v(53.22, -24.62) * mm, "end": v(54, -26.26) * mm});
            skLineSegment(sketch, "E292", {"start": v(54, -26.26) * mm, "end": v(54.46, -27.46) * mm});
            skLineSegment(sketch, "E293", {"start": v(54.46, -27.46) * mm, "end": v(54.6, -27.88) * mm});
            skLineSegment(sketch, "E294", {"start": v(54.6, -27.88) * mm, "end": v(55.04, -27.6) * mm});
            skLineSegment(sketch, "E295", {"start": v(55.04, -27.6) * mm, "end": v(56.07, -26.26) * mm});
            skLineSegment(sketch, "E296", {"start": v(56.07, -26.26) * mm, "end": v(57.1, -24.02) * mm});
            skLineSegment(sketch, "E297", {"start": v(57.1, -24.02) * mm, "end": v(57.96, -21.62) * mm});
            skLineSegment(sketch, "E298", {"start": v(57.96, -21.62) * mm, "end": v(58.64, -20.02) * mm});
            skLineSegment(sketch, "E299", {"start": v(58.64, -20.02) * mm, "end": v(58.96, -19.55) * mm});
            skLineSegment(sketch, "E300", {"start": v(58.96, -19.55) * mm, "end": v(59.28, -19.06) * mm});
            skLineSegment(sketch, "E301", {"start": v(59.28, -19.06) * mm, "end": v(60.8, -17.93) * mm});
            skLineSegment(sketch, "E302", {"start": v(60.8, -17.93) * mm, "end": v(63.23, -17.22) * mm});
            skLineSegment(sketch, "E303", {"start": v(63.23, -17.22) * mm, "end": v(66, -17.06) * mm});
            skLineSegment(sketch, "E304", {"start": v(66, -17.06) * mm, "end": v(68.12, -17.1) * mm});
            skLineSegment(sketch, "E305", {"start": v(68.12, -17.1) * mm, "end": v(68.83, -17.1) * mm});
            skLineSegment(sketch, "E306", {"start": v(68.83, -17.1) * mm, "end": v(69.19, -17.11) * mm});
            skLineSegment(sketch, "E307", {"start": v(69.19, -17.11) * mm, "end": v(70.26, -17.17) * mm});
            skLineSegment(sketch, "E308", {"start": v(70.26, -17.17) * mm, "end": v(71.7, -17.33) * mm});
            skLineSegment(sketch, "E309", {"start": v(71.7, -17.33) * mm, "end": v(73.09, -17.64) * mm});
            skLineSegment(sketch, "E310", {"start": v(73.09, -17.64) * mm, "end": v(74.33, -18.13) * mm});
            skLineSegment(sketch, "E311", {"start": v(74.33, -18.13) * mm, "end": v(75.36, -18.82) * mm});
            skLineSegment(sketch, "E312", {"start": v(75.36, -18.82) * mm, "end": v(76.1, -19.76) * mm});
            skLineSegment(sketch, "E313", {"start": v(76.1, -19.76) * mm, "end": v(76.46, -20.98) * mm});
            skLineSegment(sketch, "E314", {"start": v(76.46, -20.98) * mm, "end": v(76.45, -22.14) * mm});
            skLineSegment(sketch, "E315", {"start": v(76.45, -22.14) * mm, "end": v(76.38, -22.52) * mm});
            skLineSegment(sketch, "E316", {"start": v(76.38, -22.52) * mm, "end": v(76.25, -23.2) * mm});
            skLineSegment(sketch, "E317", {"start": v(76.25, -23.2) * mm, "end": v(75.71, -25.23) * mm});
            skLineSegment(sketch, "E318", {"start": v(75.71, -25.23) * mm, "end": v(74.8, -28.07) * mm});
            skLineSegment(sketch, "E319", {"start": v(74.8, -28.07) * mm, "end": v(73.78, -30.9) * mm});
            skLineSegment(sketch, "E320", {"start": v(73.78, -30.9) * mm, "end": v(73.05, -32.89) * mm});
            skLineSegment(sketch, "E321", {"start": v(73.05, -32.89) * mm, "end": v(72.82, -33.56) * mm});
            skLineSegment(sketch, "E322", {"start": v(72.82, -33.56) * mm, "end": v(72.47, -34.54) * mm});
            skLineSegment(sketch, "E323", {"start": v(72.47, -34.54) * mm, "end": v(68.58, -44.27) * mm});
            skLineSegment(sketch, "E324", {"start": v(68.58, -44.27) * mm, "end": v(68.15, -45.21) * mm});
            skLineSegment(sketch, "E325", {"start": v(68.15, -45.21) * mm, "end": v(68.05, -45.45) * mm});
            skLineSegment(sketch, "E326", {"start": v(68.05, -45.45) * mm, "end": v(67.75, -46.15) * mm});
            skLineSegment(sketch, "E327", {"start": v(67.75, -46.15) * mm, "end": v(67.38, -47.04) * mm});
            skLineSegment(sketch, "E328", {"start": v(67.38, -47.04) * mm, "end": v(67, -47.86) * mm});
            skLineSegment(sketch, "E329", {"start": v(67, -47.86) * mm, "end": v(66.55, -48.62) * mm});
            skLineSegment(sketch, "E330", {"start": v(66.55, -48.62) * mm, "end": v(66, -49.28) * mm});
            skLineSegment(sketch, "E331", {"start": v(66, -49.28) * mm, "end": v(65.31, -49.84) * mm});
            skLineSegment(sketch, "E332", {"start": v(65.31, -49.84) * mm, "end": v(64.43, -50.27) * mm});
            skLineSegment(sketch, "E333", {"start": v(64.43, -50.27) * mm, "end": v(63.6, -50.52) * mm});
            skLineSegment(sketch, "E334", {"start": v(63.6, -50.52) * mm, "end": v(63.32, -50.58) * mm});
            skLineSegment(sketch, "E335", {"start": v(63.32, -50.58) * mm, "end": v(62.62, -50.7) * mm});
            skLineSegment(sketch, "E336", {"start": v(62.62, -50.7) * mm, "end": v(60.52, -50.98) * mm});
            skLineSegment(sketch, "E337", {"start": v(60.52, -50.98) * mm, "end": v(57.36, -51.16) * mm});
            skLineSegment(sketch, "E338", {"start": v(57.36, -51.16) * mm, "end": v(54.24, -50.97) * mm});
            skLineSegment(sketch, "E339", {"start": v(54.24, -50.97) * mm, "end": v(52.18, -50.54) * mm});
            skLineSegment(sketch, "E340", {"start": v(52.18, -50.54) * mm, "end": v(51.55, -50.26) * mm});
            skLineSegment(sketch, "E341", {"start": v(51.55, -50.26) * mm, "end": v(50.88, -49.97) * mm});
            skLineSegment(sketch, "E342", {"start": v(50.88, -49.97) * mm, "end": v(49.1, -48.6) * mm});
            skLineSegment(sketch, "E343", {"start": v(49.1, -48.6) * mm, "end": v(47.05, -46.24) * mm});
            skLineSegment(sketch, "E344", {"start": v(47.05, -46.24) * mm, "end": v(45.22, -43.65) * mm});
            skLineSegment(sketch, "E345", {"start": v(45.22, -43.65) * mm, "end": v(43.9, -41.81) * mm});
            skLineSegment(sketch, "E346", {"start": v(43.9, -41.81) * mm, "end": v(43.42, -41.25) * mm});
            skLineSegment(sketch, "E347", {"start": v(43.42, -41.25) * mm, "end": v(43.04, -41.77) * mm});
            skLineSegment(sketch, "E348", {"start": v(43.04, -41.77) * mm, "end": v(42.04, -43.44) * mm});
            skLineSegment(sketch, "E349", {"start": v(42.04, -43.44) * mm, "end": v(40.69, -45.8) * mm});
            skLineSegment(sketch, "E350", {"start": v(40.69, -45.8) * mm, "end": v(39.2, -48.05) * mm});
            skLineSegment(sketch, "E351", {"start": v(39.2, -48.05) * mm, "end": v(37.9, -49.5) * mm});
            skLineSegment(sketch, "E352", {"start": v(37.9, -49.5) * mm, "end": v(37.39, -49.87) * mm});
            skLineSegment(sketch, "E353", {"start": v(37.39, -49.87) * mm, "end": v(36.97, -50.18) * mm});
            skLineSegment(sketch, "E354", {"start": v(36.97, -50.18) * mm, "end": v(35.44, -50.76) * mm});
            skLineSegment(sketch, "E355", {"start": v(35.44, -50.76) * mm, "end": v(32.97, -51.18) * mm});
            skLineSegment(sketch, "E356", {"start": v(32.97, -51.18) * mm, "end": v(30.33, -51.28) * mm});
            skLineSegment(sketch, "E357", {"start": v(30.33, -51.28) * mm, "end": v(28.47, -51.22) * mm});
            skLineSegment(sketch, "E358", {"start": v(28.47, -51.22) * mm, "end": v(27.86, -51.18) * mm});
            skLineSegment(sketch, "E359", {"start": v(27.86, -51.18) * mm, "end": v(27.28, -51.13) * mm});
            skLineSegment(sketch, "E360", {"start": v(27.28, -51.13) * mm, "end": v(25.56, -50.56) * mm});
            skLineSegment(sketch, "E361", {"start": v(25.56, -50.56) * mm, "end": v(23.8, -49.2) * mm});
            skLineSegment(sketch, "E362", {"start": v(23.8, -49.2) * mm, "end": v(22.46, -47.26) * mm});
            skLineSegment(sketch, "E363", {"start": v(22.46, -47.26) * mm, "end": v(21.47, -44.91) * mm});
            skLineSegment(sketch, "E364", {"start": v(21.47, -44.91) * mm, "end": v(20.72, -42.34) * mm});
            skLineSegment(sketch, "E365", {"start": v(20.72, -42.34) * mm, "end": v(20.11, -39.71) * mm});
            skLineSegment(sketch, "E366", {"start": v(20.11, -39.71) * mm, "end": v(19.56, -37.2) * mm});
            skLineSegment(sketch, "E367", {"start": v(19.56, -37.2) * mm, "end": v(19.14, -35.54) * mm});
            skLineSegment(sketch, "E368", {"start": v(19.14, -35.54) * mm, "end": v(18.96, -35) * mm});
            skLineSegment(sketch, "E369", {"start": v(18.96, -35) * mm, "end": v(18.8, -34.48) * mm});
            skLineSegment(sketch, "E370", {"start": v(18.8, -34.48) * mm, "end": v(18.21, -32.96) * mm});
            skLineSegment(sketch, "E371", {"start": v(18.21, -32.96) * mm, "end": v(17.24, -30.47) * mm});
            skLineSegment(sketch, "E372", {"start": v(17.24, -30.47) * mm, "end": v(16.25, -27.7) * mm});
            skLineSegment(sketch, "E373", {"start": v(16.25, -27.7) * mm, "end": v(15.45, -24.87) * mm});
            skLineSegment(sketch, "E374", {"start": v(15.45, -24.87) * mm, "end": v(15.04, -22.15) * mm});
            skLineSegment(sketch, "E375", {"start": v(15.04, -22.15) * mm, "end": v(15.25, -19.74) * mm});
            skLineSegment(sketch, "E376", {"start": v(15.25, -19.74) * mm, "end": v(16.28, -17.84) * mm});
            skLineSegment(sketch, "E377", {"start": v(16.28, -17.84) * mm, "end": v(17.78, -16.8) * mm});
            skLineSegment(sketch, "E378", {"start": v(17.78, -16.8) * mm, "end": v(18.33, -16.63) * mm});
            skLineSegment(sketch, "E379", {"start": v(18.33, -16.63) * mm, "end": v(18.98, -16.43) * mm});
            skLineSegment(sketch, "E380", {"start": v(18.98, -16.43) * mm, "end": v(20.98, -16.06) * mm});
            skLineSegment(sketch, "E381", {"start": v(20.98, -16.06) * mm, "end": v(23.87, -15.82) * mm});
            skLineSegment(sketch, "E382", {"start": v(23.87, -15.82) * mm, "end": v(26.77, -15.91) * mm});
            skLineSegment(sketch, "E383", {"start": v(26.77, -15.91) * mm, "end": v(28.78, -16.18) * mm});
            skLineSegment(sketch, "E384", {"start": v(28.78, -16.18) * mm, "end": v(29.44, -16.33) * mm});
            skLineSegment(sketch, "E385", {"start": v(29.44, -16.33) * mm, "end": v(29.84, -16.43) * mm});
            skLineSegment(sketch, "E386", {"start": v(29.84, -16.43) * mm, "end": v(31.02, -16.91) * mm});
            skLineSegment(sketch, "E387", {"start": v(31.02, -16.91) * mm, "end": v(32.27, -17.78) * mm});
            skLineSegment(sketch, "E388", {"start": v(32.27, -17.78) * mm, "end": v(33.24, -18.9) * mm});
            skLineSegment(sketch, "E389", {"start": v(33.24, -18.9) * mm, "end": v(34, -20.2) * mm});
            skLineSegment(sketch, "E390", {"start": v(34, -20.2) * mm, "end": v(34.63, -21.62) * mm});
            skLineSegment(sketch, "E391", {"start": v(34.63, -21.62) * mm, "end": v(35.18, -23.13) * mm});
            skLineSegment(sketch, "E392", {"start": v(35.18, -23.13) * mm, "end": v(35.72, -24.67) * mm});
            skLineSegment(sketch, "E393", {"start": v(35.72, -24.67) * mm, "end": v(36.15, -25.8) * mm});
            skLineSegment(sketch, "E394", {"start": v(36.15, -25.8) * mm, "end": v(36.3, -26.18) * mm});
            skLineSegment(sketch, "E395", {"start": v(36.3, -26.18) * mm, "end": v(36.44, -26.07) * mm});
            skLineSegment(sketch, "E396", {"start": v(36.44, -26.07) * mm, "end": v(36.8, -25.67) * mm});
            skLineSegment(sketch, "E397", {"start": v(36.8, -25.67) * mm, "end": v(37.52, -24.84) * mm});
            skLineSegment(sketch, "E398", {"start": v(37.52, -24.84) * mm, "end": v(38.43, -23.8) * mm});
            skLineSegment(sketch, "E399", {"start": v(38.43, -23.8) * mm, "end": v(39.5, -22.65) * mm});
            skLineSegment(sketch, "E400", {"start": v(39.5, -22.65) * mm, "end": v(40.68, -21.52) * mm});
            skLineSegment(sketch, "E401", {"start": v(40.68, -21.52) * mm, "end": v(41.97, -20.5) * mm});
            skLineSegment(sketch, "E402", {"start": v(41.97, -20.5) * mm, "end": v(43.31, -19.72) * mm});
            skLineSegment(sketch, "E403", {"start": v(43.31, -19.72) * mm, "end": v(44.33, -19.33) * mm});
            skLineSegment(sketch, "E404", {"start": v(44.33, -19.33) * mm, "end": v(44.68, -19.27) * mm});
            skSolve(sketch);
        }
        {
            var Q0;
            Q0 = qSketchRegion(id + "F0", true);
            extrude(context, id + "F1", {"entities" : qUnion([Q0]), "depth" : 15 * mm, "offsetDistance" : 25 * mm});
        }
        {
            var Q0;
            Q0=makeQuery(id+"F1.opExtrude","CAP_FACE",FACE,{"disambiguationData":[OSD([sQuery(id+"F0.wireOp",EDGE,"E102"),sQuery(id+"F0.wireOp",EDGE,"E103"),sQuery(id+"F0.wireOp",EDGE,"E104"),sQuery(id+"F0.wireOp",EDGE,"E105"),sQuery(id+"F0.wireOp",EDGE,"E106"),sQuery(id+"F0.wireOp",EDGE,"E107"),sQuery(id+"F0.wireOp",EDGE,"E108"),sQuery(id+"F0.wireOp",EDGE,"E109"),sQuery(id+"F0.wireOp",EDGE,"E110"),sQuery(id+"F0.wireOp",EDGE,"E111"),sQuery(id+"F0.wireOp",EDGE,"E112"),sQuery(id+"F0.wireOp",EDGE,"E113"),sQuery(id+"F0.wireOp",EDGE,"E114"),sQuery(id+"F0.wireOp",EDGE,"E115"),sQuery(id+"F0.wireOp",EDGE,"E116"),sQuery(id+"F0.wireOp",EDGE,"E117"),sQuery(id+"F0.wireOp",EDGE,"E118"),sQuery(id+"F0.wireOp",EDGE,"E119"),sQuery(id+"F0.wireOp",EDGE,"E120"),sQuery(id+"F0.wireOp",EDGE,"E121"),sQuery(id+"F0.wireOp",EDGE,"E122"),sQuery(id+"F0.wireOp",EDGE,"E123"),sQuery(id+"F0.wireOp",EDGE,"E124"),sQuery(id+"F0.wireOp",EDGE,"E125"),sQuery(id+"F0.wireOp",EDGE,"E126"),sQuery(id+"F0.wireOp",EDGE,"E127"),sQuery(id+"F0.wireOp",EDGE,"E128"),sQuery(id+"F0.wireOp",EDGE,"E129"),sQuery(id+"F0.wireOp",EDGE,"E130"),sQuery(id+"F0.wireOp",EDGE,"E131"),sQuery(id+"F0.wireOp",EDGE,"E132"),sQuery(id+"F0.wireOp",EDGE,"E133"),sQuery(id+"F0.wireOp",EDGE,"E134"),sQuery(id+"F0.wireOp",EDGE,"E135"),sQuery(id+"F0.wireOp",EDGE,"E136"),sQuery(id+"F0.wireOp",EDGE,"E137"),sQuery(id+"F0.wireOp",EDGE,"E138"),sQuery(id+"F0.wireOp",EDGE,"E139"),sQuery(id+"F0.wireOp",EDGE,"E140"),sQuery(id+"F0.wireOp",EDGE,"E141"),sQuery(id+"F0.wireOp",EDGE,"E142"),sQuery(id+"F0.wireOp",EDGE,"E143"),sQuery(id+"F0.wireOp",EDGE,"E144"),sQuery(id+"F0.wireOp",EDGE,"E145"),sQuery(id+"F0.wireOp",EDGE,"E146"),sQuery(id+"F0.wireOp",EDGE,"E147"),sQuery(id+"F0.wireOp",EDGE,"E148"),sQuery(id+"F0.wireOp",EDGE,"E149"),sQuery(id+"F0.wireOp",EDGE,"E150"),sQuery(id+"F0.wireOp",EDGE,"E151"),sQuery(id+"F0.wireOp",EDGE,"E152"),sQuery(id+"F0.wireOp",EDGE,"E153"),sQuery(id+"F0.wireOp",EDGE,"E154"),sQuery(id+"F0.wireOp",EDGE,"E155"),sQuery(id+"F0.wireOp",EDGE,"E156"),sQuery(id+"F0.wireOp",EDGE,"E157"),sQuery(id+"F0.wireOp",EDGE,"E158"),sQuery(id+"F0.wireOp",EDGE,"E159"),sQuery(id+"F0.wireOp",EDGE,"E160"),sQuery(id+"F0.wireOp",EDGE,"E161"),sQuery(id+"F0.wireOp",EDGE,"E162"),sQuery(id+"F0.wireOp",EDGE,"E163"),sQuery(id+"F0.wireOp",EDGE,"E164"),sQuery(id+"F0.wireOp",EDGE,"E165"),sQuery(id+"F0.wireOp",EDGE,"E166"),sQuery(id+"F0.wireOp",EDGE,"E167"),sQuery(id+"F0.wireOp",EDGE,"E168"),sQuery(id+"F0.wireOp",EDGE,"E169"),sQuery(id+"F0.wireOp",EDGE,"E170"),sQuery(id+"F0.wireOp",EDGE,"E171"),sQuery(id+"F0.wireOp",EDGE,"E172"),sQuery(id+"F0.wireOp",EDGE,"E173"),sQuery(id+"F0.wireOp",EDGE,"E174"),sQuery(id+"F0.wireOp",EDGE,"E175"),sQuery(id+"F0.wireOp",EDGE,"E176"),sQuery(id+"F0.wireOp",EDGE,"E177"),sQuery(id+"F0.wireOp",EDGE,"E178"),sQuery(id+"F0.wireOp",EDGE,"E179"),sQuery(id+"F0.wireOp",EDGE,"E180"),sQuery(id+"F0.wireOp",EDGE,"E181"),sQuery(id+"F0.wireOp",EDGE,"E182"),sQuery(id+"F0.wireOp",EDGE,"E183"),sQuery(id+"F0.wireOp",EDGE,"E184"),sQuery(id+"F0.wireOp",EDGE,"E185"),sQuery(id+"F0.wireOp",EDGE,"E186"),sQuery(id+"F0.wireOp",EDGE,"E187"),sQuery(id+"F0.wireOp",EDGE,"E188"),sQuery(id+"F0.wireOp",EDGE,"E189"),sQuery(id+"F0.wireOp",EDGE,"E190"),sQuery(id+"F0.wireOp",EDGE,"E191"),sQuery(id+"F0.wireOp",EDGE,"E192"),sQuery(id+"F0.wireOp",EDGE,"E193"),sQuery(id+"F0.wireOp",EDGE,"E194"),sQuery(id+"F0.wireOp",EDGE,"E195"),sQuery(id+"F0.wireOp",EDGE,"E196"),sQuery(id+"F0.wireOp",EDGE,"E197"),sQuery(id+"F0.wireOp",EDGE,"E198"),sQuery(id+"F0.wireOp",EDGE,"E199"),sQuery(id+"F0.wireOp",EDGE,"E200"),sQuery(id+"F0.wireOp",EDGE,"E201"),sQuery(id+"F0.wireOp",EDGE,"E202"),sQuery(id+"F0.wireOp",EDGE,"E203"),sQuery(id+"F0.wireOp",EDGE,"E204"),sQuery(id+"F0.wireOp",EDGE,"E205"),sQuery(id+"F0.wireOp",EDGE,"E206"),sQuery(id+"F0.wireOp",EDGE,"E207"),sQuery(id+"F0.wireOp",EDGE,"E208"),sQuery(id+"F0.wireOp",EDGE,"E209"),sQuery(id+"F0.wireOp",EDGE,"E210"),sQuery(id+"F0.wireOp",EDGE,"E211"),sQuery(id+"F0.wireOp",EDGE,"E212"),sQuery(id+"F0.wireOp",EDGE,"E213"),sQuery(id+"F0.wireOp",EDGE,"E214"),sQuery(id+"F0.wireOp",EDGE,"E215"),sQuery(id+"F0.wireOp",EDGE,"E216"),sQuery(id+"F0.wireOp",EDGE,"E217"),sQuery(id+"F0.wireOp",EDGE,"E218"),sQuery(id+"F0.wireOp",EDGE,"E219"),sQuery(id+"F0.wireOp",EDGE,"E220"),sQuery(id+"F0.wireOp",EDGE,"E221"),sQuery(id+"F0.wireOp",EDGE,"E222"),sQuery(id+"F0.wireOp",EDGE,"E223"),sQuery(id+"F0.wireOp",EDGE,"E224"),sQuery(id+"F0.wireOp",EDGE,"E225"),sQuery(id+"F0.wireOp",EDGE,"E226"),sQuery(id+"F0.wireOp",EDGE,"E227"),sQuery(id+"F0.wireOp",EDGE,"E228"),sQuery(id+"F0.wireOp",EDGE,"E229"),sQuery(id+"F0.wireOp",EDGE,"E230"),sQuery(id+"F0.wireOp",EDGE,"E231"),sQuery(id+"F0.wireOp",EDGE,"E232"),sQuery(id+"F0.wireOp",EDGE,"E233"),sQuery(id+"F0.wireOp",EDGE,"E234"),sQuery(id+"F0.wireOp",EDGE,"E235"),sQuery(id+"F0.wireOp",EDGE,"E236"),sQuery(id+"F0.wireOp",EDGE,"E237"),sQuery(id+"F0.wireOp",EDGE,"E238"),sQuery(id+"F0.wireOp",EDGE,"E239"),sQuery(id+"F0.wireOp",EDGE,"E240"),sQuery(id+"F0.wireOp",EDGE,"E241"),sQuery(id+"F0.wireOp",EDGE,"E242"),sQuery(id+"F0.wireOp",EDGE,"E243"),sQuery(id+"F0.wireOp",EDGE,"E244"),sQuery(id+"F0.wireOp",EDGE,"E245"),sQuery(id+"F0.wireOp",EDGE,"E246"),sQuery(id+"F0.wireOp",EDGE,"E247"),sQuery(id+"F0.wireOp",EDGE,"E248"),sQuery(id+"F0.wireOp",EDGE,"E249"),sQuery(id+"F0.wireOp",EDGE,"E250"),sQuery(id+"F0.wireOp",EDGE,"E251"),sQuery(id+"F0.wireOp",EDGE,"E252"),sQuery(id+"F0.wireOp",EDGE,"E253"),sQuery(id+"F0.wireOp",EDGE,"E254"),sQuery(id+"F0.wireOp",EDGE,"E255"),sQuery(id+"F0.wireOp",EDGE,"E256"),sQuery(id+"F0.wireOp",EDGE,"E257"),sQuery(id+"F0.wireOp",EDGE,"E258"),sQuery(id+"F0.wireOp",EDGE,"E259"),sQuery(id+"F0.wireOp",EDGE,"E260"),sQuery(id+"F0.wireOp",EDGE,"E261"),sQuery(id+"F0.wireOp",EDGE,"E262"),sQuery(id+"F0.wireOp",EDGE,"E263"),sQuery(id+"F0.wireOp",EDGE,"E264"),sQuery(id+"F0.wireOp",EDGE,"E265"),sQuery(id+"F0.wireOp",EDGE,"E266"),sQuery(id+"F0.wireOp",EDGE,"E267"),sQuery(id+"F0.wireOp",EDGE,"E268"),sQuery(id+"F0.wireOp",EDGE,"E269"),sQuery(id+"F0.wireOp",EDGE,"E270"),sQuery(id+"F0.wireOp",EDGE,"E271"),sQuery(id+"F0.wireOp",EDGE,"E272"),sQuery(id+"F0.wireOp",EDGE,"E273"),sQuery(id+"F0.wireOp",EDGE,"E274"),sQuery(id+"F0.wireOp",EDGE,"E275"),sQuery(id+"F0.wireOp",EDGE,"E276"),sQuery(id+"F0.wireOp",EDGE,"E277"),sQuery(id+"F0.wireOp",EDGE,"E278"),sQuery(id+"F0.wireOp",EDGE,"E279"),sQuery(id+"F0.wireOp",EDGE,"E280"),sQuery(id+"F0.wireOp",EDGE,"E281"),sQuery(id+"F0.wireOp",EDGE,"E282"),sQuery(id+"F0.wireOp",EDGE,"E283")])],"isStart":false});
            var sketch = newSketch(context, id + "F2", { "sketchPlane" : qUnion([Q0])});
            skLineSegment(sketch, "E405.bottom", {"start": v(0.54, 66.24) * mm, "end": v(43.04, 66.24) * mm});
            skLineSegment(sketch, "E405.top", {"start": v(-107.06, -67.4) * mm, "end": v(108.14, -67.4) * mm});
            skLineSegment(sketch, "E405.left", {"start": v(-107.06, -15.3) * mm, "end": v(-107.06, -67.4) * mm});
            skLineSegment(sketch, "E405.right", {"start": v(108.14, -0.58) * mm, "end": v(108.14, -67.4) * mm});
            skLineSegment(sketch, "E406", {"start": v(-107.06, -15.3) * mm, "end": v(0.54, 66.24) * mm});
            skLineSegment(sketch, "E407", {"start": v(-17.73, 83.7) * mm, "end": v(-17.73, 83.7) * mm});
            skLineSegment(sketch, "E408", {"start": v(43.04, 66.24) * mm, "end": v(108.14, -0.58) * mm});
            skPoint(sketch, "E409.orphan", {"position": v(108.14, 66.24) * mm});
            skPoint(sketch, "E410.orphan", {"position": v(-107.06, 66.24) * mm});
            skSolve(sketch);
        }
        {
            var Q0;
            Q0 = qSketchRegion(id + "F2", true);
            extrude(context, id + "F3", {"entities" : qUnion([Q0]), "depth" : 25 * mm, "offsetDistance" : 25 * mm});
        }
    });
